FCSTD DOCUMENT  (FreeCAD 1.0R39319 (Git))
Label: project-cut-door-spacer
License: All rights reserved
LicenseURL: http://en.wikipedia.org/wiki/All_rights_reserved
objects: Sketcher::SketchObject×1, App::VarSet×1, PartDesign::Body×1, TechDraw::DrawSVGTemplate×1, TechDraw::DrawProjGroupItem×1, TechDraw::DrawPage×1
note: 3 computed .brp shape members not serialized (recipe doc carries the construction recipe); baked Part::Feature solids carry a one-line shape summary decoded from their .brp

FEATURE [Sketcher::SketchObject] Sketch
  ArcFitTolerance = 1e-06
  AttachmentSupport = -> [XY_Plane]
  FullyConstrained = true
  MakeInternals = false
  MapMode = 5
  expr: Constraints[22] = VarSet.width
  sketch-geometry (15):
    g0: LineSegment StartX=1 StartY=0 StartZ=0 EndX=34 EndY=0 EndZ=0
    g1: LineSegment StartX=35 StartY=1 StartZ=0 EndX=35 EndY=113 EndZ=0
    g2: LineSegment StartX=34 StartY=114 StartZ=0 EndX=1 EndY=114 EndZ=0
    g3: LineSegment StartX=0 StartY=113 StartZ=0 EndX=0 EndY=1 EndZ=0
    g4: ArcOfCircle CenterX=1 CenterY=1 CenterZ=0 NormalX=0 NormalY=0 NormalZ=1 AngleXU=0 Radius=1 StartAngle=3.14159 EndAngle=4.71239
    g5: ArcOfCircle CenterX=34 CenterY=1 CenterZ=0 NormalX=0 NormalY=0 NormalZ=1 AngleXU=0 Radius=1 StartAngle=4.71239 EndAngle=6.28319
    g6: ArcOfCircle CenterX=34 CenterY=113 CenterZ=0 NormalX=0 NormalY=0 NormalZ=1 AngleXU=0 Radius=1 StartAngle=-6.2e-15 EndAngle=1.5708
    g7: ArcOfCircle CenterX=1 CenterY=113 CenterZ=0 NormalX=0 NormalY=0 NormalZ=1 AngleXU=0 Radius=1 StartAngle=1.5708 EndAngle=3.14159
    g8: GeomPoint [constr] X=0 Y=0 Z=0
    g9: GeomPoint [constr] X=35 Y=114 Z=0
    g10: Circle CenterX=9 CenterY=73 CenterZ=0 NormalX=0 NormalY=0 NormalZ=1 AngleXU=0 Radius=4.25
    g11: Circle CenterX=26 CenterY=101 CenterZ=0 NormalX=0 NormalY=0 NormalZ=1 AngleXU=0 Radius=4.25
    g12: Circle CenterX=9 CenterY=41 CenterZ=0 NormalX=0 NormalY=0 NormalZ=1 AngleXU=0 Radius=4.25
    g13: Circle CenterX=26 CenterY=13 CenterZ=0 NormalX=0 NormalY=0 NormalZ=1 AngleXU=0 Radius=4.25
    g14: LineSegment [constr] StartX=0 StartY=57 StartZ=0 EndX=35 EndY=57 EndZ=0
  constraints (35):
    c: Tangent(g0,g4) = -1.5708
    c: Tangent(g0,g5) = -1.5708
    c: Tangent(g1,g5) = -1.5708
    c: Tangent(g1,g6) = -1.5708
    c: Tangent(g2,g6) = -1.5708
    c: Tangent(g2,g7) = -1.5708
    c: Tangent(g3,g7) = -1.5708
    c: Tangent(g3,g4) = -1.5708
    c: Horizontal(g0)
    c: Horizontal(g2)
    c: Vertical(g1)
    c: Vertical(g3)
    c: Equal(g4,g5)
    c: Equal(g5,g6)
    c: Equal(g6,g7)
    c: PointOnObject(g8,g0)
    c: PointOnObject(g8,g3)
    c: PointOnObject(g9,g1)
    c: PointOnObject(g9,g2)
    c: Radius(g5) = 1
    c: Coincident(g8,g-1)
    c: Distance(g0,g2) = 114
    c: Distance(g3,g1) = 35
    c: Diameter(g10) = 8.5
    c: DistanceY(g10,g2) = 41
    c: DistanceX(g-1,g10) = 9
    c: Distance(g11,g2) = 13
    c: DistanceX(g-1,g11) = 26
    c: Equal(g10,g11)
    c: Equal(g11,g12)
    c: Equal(g12,g13)
    c: Symmetric(g3,g3,g14)
    c: Symmetric(g1,g1,g14)
    c: Symmetric(g10,g12,g14)
    c: Symmetric(g11,g13,g14)
FEATURE [App::VarSet] VarSet
  height = 114
  width = 35
FEATURE [PartDesign::Body] Body
  AllowCompound = false
  Group = -> [Sketch,VarSet]
  Origin = -> Origin
FEATURE [TechDraw::DrawSVGTemplate] Template
  Height = 215.9
  Orientation = 1
  Template = /app/share/Mod/TechDraw/Templates/USLetter_Landscape_blank.svg
  Width = 279.4
FEATURE [TechDraw::DrawProjGroupItem] View  label="Spacer"
  CoarseView = false
  Direction = (0,0,1)
  Focus = 100
  HardHidden = false
  IsoCount = 0
  IsoHidden = false
  IsoVisible = false
  LockPosition = false
  Perspective = false
  Rotation = 0
  RotationVector = (1,0,0)
  ScaleType = 0
  ScrubCount = 1
  SeamHidden = false
  SeamVisible = true
  SmoothHidden = false
  SmoothVisible = true
  Source = -> [Sketch]
  Type = 0
  X = 58.2828
  XDirection = (1,0,0)
  Y = 133.89
FEATURE [TechDraw::DrawPage] Page
  KeepUpdated = true
  NextBalloonIndex = 1
  ProjectionType = 0
  Template = -> Template
  Views = -> [View]
